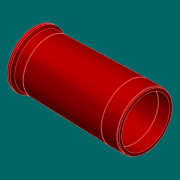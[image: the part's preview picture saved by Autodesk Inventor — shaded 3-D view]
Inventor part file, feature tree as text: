
AUTODESK INVENTOR PART (.ipt)
format: ipt  version: 2017.3 (Build 213256000, 256)  size: 181,760 bytes
history: native  units: in
note: dims shown in document units (in); Inventor stores cm internally (conversion verified against a paired STEP export)
features: revolve x1, fillet x1, sketch x1
ambient origin geometry x8: Origin, YZ Plane, XZ Plane, XY Plane, X Axis, Y Axis, Z Axis, Center Point
bodies: Solid1 (feature_tree)
feature tree (3):
  revolve  "Revolution1"  [1 undecoded]
  fillet  "Fillet1"  Radius=28.5in
  sketch  "Sketch1"  dims[d0=55.9843in d1=26.0in d2=28.5in d3=32.23in d4=2.0in d5=1.0in d6=1.0in d7=32.48in d8=30.0in d9=1.0in d10=4.0in d11=12.0in d12=12.0in d13=48.0in d14=2.0779in d15=90.0deg d16=0.0312in d17=1.0in d18=45.0deg d19=32.75in d23=1.0in d24=45.0deg d25=32.75in]
note: 1 required parameter value undecoded (feature->parameter linkage not recoverable at this tier; creation-order binding heuristic only, values carry confidence <= 0.55)
